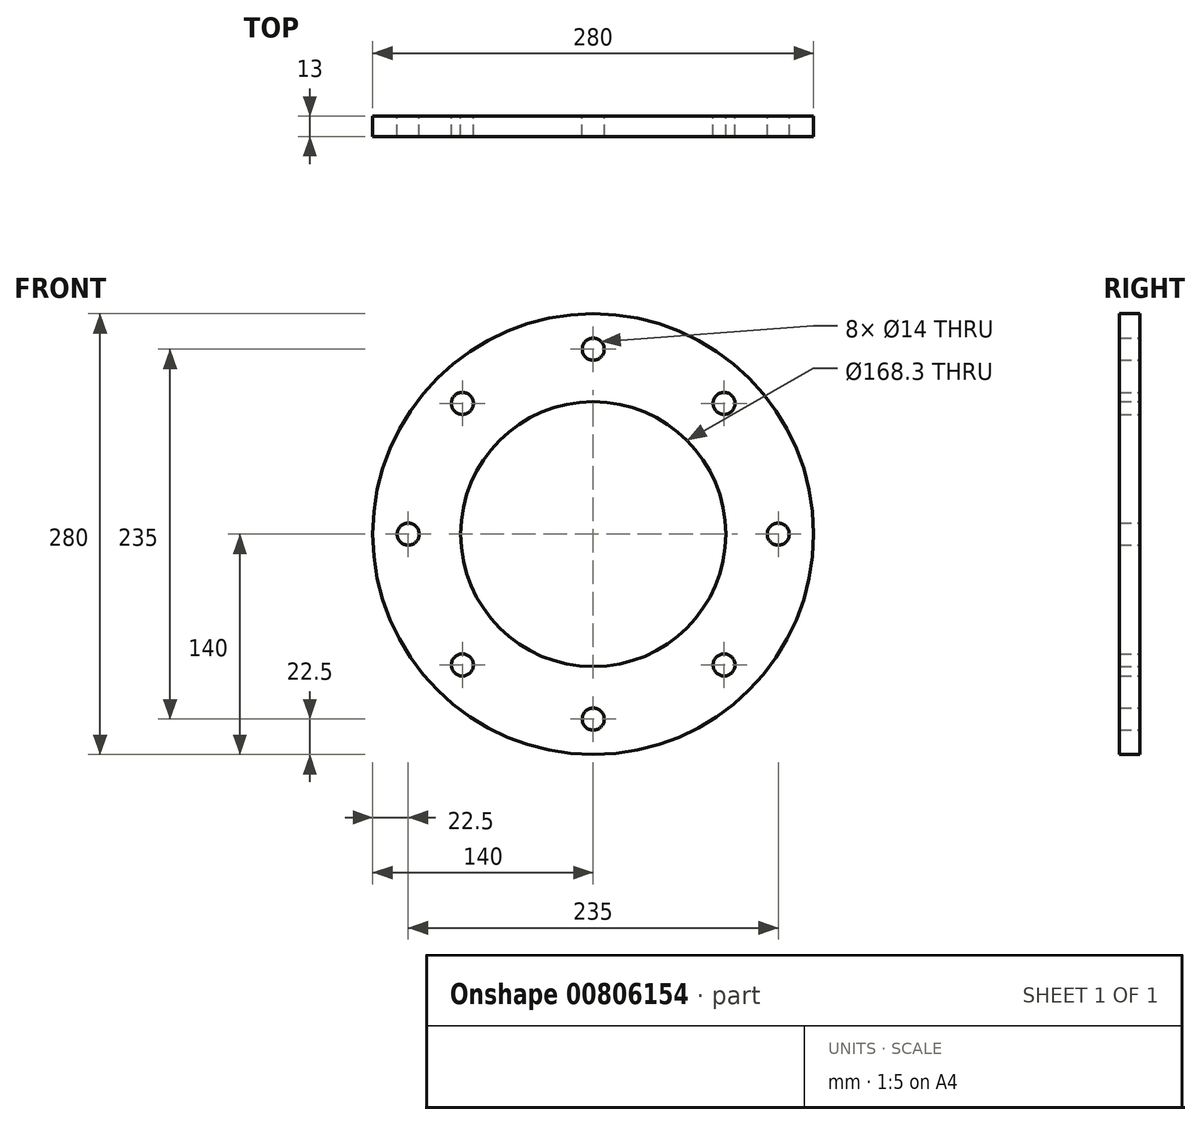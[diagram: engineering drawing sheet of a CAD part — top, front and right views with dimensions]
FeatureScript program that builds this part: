
annotation { "Feature Type Name" : "Feature", "Feature Type Description" : "" }
export const myFeature = defineFeature(function(context is Context, id is Id, definition is map)
    precondition{}
    {
        {
            var Q0;
            Q0=qCreatedBy(makeId("Front.planeOp"),FACE);
            var sketch = newSketch(context, id + "F0", { "sketchPlane" : qUnion([Q0])});
            skCircle(sketch, "E0", {"center": v(0, 0) * mm, "radius": 140 * mm});
            skCircle(sketch, "E1", {"center": v(0, 0) * mm, "radius": 117.5 * mm});
            skLineSegment(sketch, "E2", {"start": v(0, 0) * mm, "end": v(140, 0) * mm});
            skCircle(sketch, "E3", {"center": v(117.5, 0) * mm, "radius": 7 * mm});
            skCircle(sketch, "E4.1.0", {"center": v(83.09, 83.09) * mm, "radius": 7 * mm});
            skCircle(sketch, "E4.2.0", {"center": v(0, 117.5) * mm, "radius": 7 * mm});
            skCircle(sketch, "E4.3.0", {"center": v(-83.09, 83.09) * mm, "radius": 7 * mm});
            skCircle(sketch, "E4.4.0", {"center": v(-117.5, 0) * mm, "radius": 7 * mm});
            skCircle(sketch, "E4.5.0", {"center": v(-83.09, -83.09) * mm, "radius": 7 * mm});
            skCircle(sketch, "E4.6.0", {"center": v(0, -117.5) * mm, "radius": 7 * mm});
            skCircle(sketch, "E4.7.0", {"center": v(83.09, -83.09) * mm, "radius": 7 * mm});
            skCircle(sketch, "E5", {"center": v(0, 0) * mm, "radius": 84.15 * mm});
            skSolve(sketch);
        }
        {
            var Q0;
            Q0=makeQuery(id+"F0.imprint","IMPRINT",FACE,{"disambiguationData":[TD([[makeQuery(id+"F0.imprint","IMPRINT",EDGE,{"derivedFrom":sQuery(id+"F0.wireOp",EDGE,"E0")}),1.0]])]});
            var Q1;
            Q1=makeQuery(id+"F0.imprint","IMPRINT",FACE,{"disambiguationData":[TD([[makeQuery(id+"F0.imprint","IMPRINT",EDGE,{"derivedFrom":sQuery(id+"F0.wireOp",EDGE,"E5")}),-1.0]])]});
            extrude(context, id + "F1", {"entities" : qUnion([Q0, Q1]), "depth" : 13 * mm, "offsetDistance" : 25 * mm});
        }
    });
